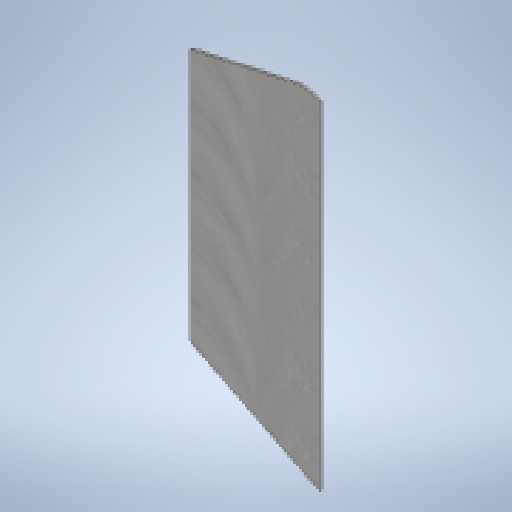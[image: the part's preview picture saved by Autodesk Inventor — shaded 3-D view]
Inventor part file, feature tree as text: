
AUTODESK INVENTOR PART (.ipt)
format: ipt  version: 2023 (Build 270158000, 158)  size: 173,056 bytes
history: native  units: mm
features: other x6, reference x5, extrude x2, sketch x2, projected_geometry x1
ambient origin geometry x8: Origin, YZ Plane, XZ Plane, XY Plane, X Axis, Y Axis, Z Axis, Center Point
bodies: Solid1 (feature_tree)
feature tree (16):
  extrude  "Extrusion1"  Depth=0.5mm TaperAngle=0.0deg
  extrude  "Extrusion2"  Depth=0.5mm
  sketch  "Sketch1"  dims[d0=0.5mm d1=0.0mm d2=0.5mm d3=0.0mm]
  reference  "Reference1"
  reference  "Reference2"
  reference  "Reference3"
  reference  "Reference4"
  reference  "Reference5"
  sketch  "Sketch2"  dims[d4=0.5mm d5=0.872665mm]
  projected_geometry  "Projected Loop1"
  other  "Assembly2"
  other  "sciana_lewa_v3:1"
  other  "pług:1"
  other  "pokrywa:1"
  other  "minisumopodsr:1"
  other  "koło_minisumo:1"
